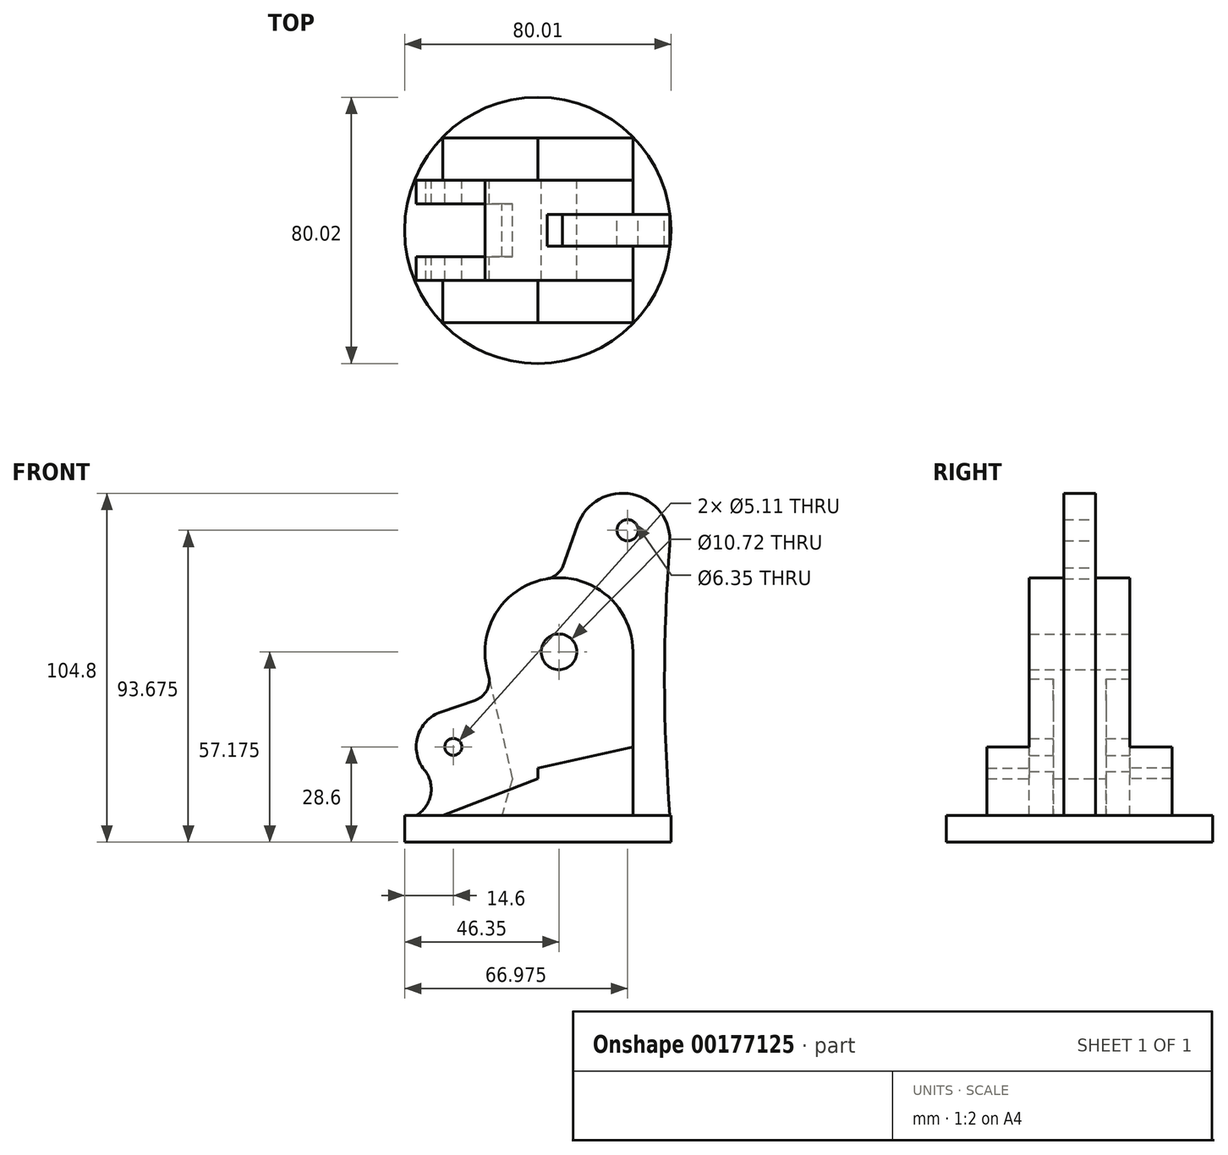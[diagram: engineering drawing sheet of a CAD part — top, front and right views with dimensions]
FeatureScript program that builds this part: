
annotation { "Feature Type Name" : "Feature", "Feature Type Description" : "" }
export const myFeature = defineFeature(function(context is Context, id is Id, definition is map)
    precondition{}
    {
        {
            var Q0;
            Q0=qCreatedBy(makeId("Front.planeOp"),FACE);
            var sketch = newSketch(context, id + "F0", { "sketchPlane" : qUnion([Q0])});
            skCircle(sketch, "E0", {"center": v(14.3, 20.65) * mm, "radius": 2.55 * mm});
            skCircle(sketch, "E1", {"center": v(46.05, 49.23) * mm, "radius": 5.36 * mm});
            skArc(sketch, "E2", {"start": v(68.28, 49.23) * mm, "mid": v(43.53, 71.3) * mm, "end": v(24.4, 44.23) * mm});
            skArc(sketch, "E3", {"start": v(10.72, 31.18) * mm, "mid": v(3.53, 23.44) * mm, "end": v(6.05, 13.19) * mm});
            skArc(sketch, "E4", {"start": v(3.17, 0) * mm, "mid": v(7.58, 6.64) * mm, "end": v(5.2, 14.26) * mm});
            skArc(sketch, "E5", {"start": v(20.84, 34.63) * mm, "mid": v(24.07, 37.1) * mm, "end": v(25.13, 41.02) * mm});
            skArc(sketch, "E6", {"start": v(42.37, 71.14) * mm, "mid": v(42.43, 71.15) * mm, "end": v(42.5, 71.16) * mm});
            skLineSegment(sketch, "E7", {"start": v(20.84, 34.63) * mm, "end": v(10.72, 31.18) * mm});
            skLineSegment(sketch, "E8", {"start": v(3.17, 0) * mm, "end": v(68.28, 0) * mm});
            skLineSegment(sketch, "E9", {"start": v(68.28, 49.23) * mm, "end": v(68.28, 0) * mm});
            skPoint(sketch, "E10.center.orphan", {"position": v(66.68, 85.73) * mm});
            skPoint(sketch, "E11.center.orphan", {"position": v(65.1, 82.55) * mm});
            skPoint(sketch, "E12.end.orphan", {"position": v(79.4, 0) * mm});
            skLineSegment(sketch, "E13", {"start": v(24.4, 44.23) * mm, "end": v(25.13, 41.02) * mm});
            skSolve(sketch);
        }
        {
            var Q0;
            Q0 = qSketchRegion(id + "F0", true);
            extrude(context, id + "F1", {"entities" : qUnion([Q0]), "endBound" : BoundingType.SYMMETRIC, "depth" : 30.18 * mm});
        }
        {
            var Q0;
            Q0=qCreatedBy(makeId("Front.planeOp"),FACE);
            var sketch = newSketch(context, id + "F2", { "sketchPlane" : qUnion([Q0])});
            skArc(sketch, "E14", {"start": v(42.5, 71.16) * mm, "mid": v(27.6, 61.62) * mm, "end": v(24.4, 44.23) * mm});
            skCircle(sketch, "E15", {"center": v(46.05, 49.23) * mm, "radius": 5.36 * mm});
            skArc(sketch, "E16", {"start": v(79.36, 81.41) * mm, "mid": v(68.1, 96.53) * mm, "end": v(51.63, 87.36) * mm});
            skArc(sketch, "E17", {"start": v(42.37, 71.14) * mm, "mid": v(45.77, 72.81) * mm, "end": v(47.62, 76.12) * mm});
            skLineSegment(sketch, "E18", {"start": v(47.03, 74.49) * mm, "end": v(51.63, 87.36) * mm});
            skLineSegment(sketch, "E19", {"start": v(24.4, 44.23) * mm, "end": v(32.04, 11.13) * mm});
            skLineSegment(sketch, "E20", {"start": v(32.04, 11.13) * mm, "end": v(28.86, 0) * mm});
            skPoint(sketch, "E20.startSnap0", {"position": v(33.4, 11.13) * mm});
            skLineSegment(sketch, "E21", {"start": v(28.86, 0) * mm, "end": v(79.4, 0) * mm});
            skArc(sketch, "E22", {"start": v(79.36, 81.41) * mm, "mid": v(77.74, 40.7) * mm, "end": v(79.4, 0) * mm});
            skCircle(sketch, "E23", {"center": v(66.68, 85.73) * mm, "radius": 3.18 * mm});
            skSolve(sketch);
        }
        {
            var Q0;
            Q0 = qSketchRegion(id + "F2", true);
            extrude(context, id + "F3", {"entities" : qUnion([Q0]), "endBound" : BoundingType.SYMMETRIC, "depth" : 9.52 * mm});
        }
        {
            var Q0;
            Q0=makeQuery(id+"FuUQKrlxmKHpC4y_2.opBoolean","SPLIT",BODY,{"disambiguationData":[OD(1.0)],"derivedFrom":makeQuery(id+"F1.opExtrude","SWEPT_BODY",BODY,{"disambiguationData":[OSD([sQuery(id+"F0.wireOp",EDGE,"E0"),sQuery(id+"F0.wireOp",EDGE,"E1"),sQuery(id+"F0.wireOp",EDGE,"E2"),sQuery(id+"F0.wireOp",EDGE,"E3"),sQuery(id+"F0.wireOp",EDGE,"E4"),sQuery(id+"F0.wireOp",EDGE,"E5"),sQuery(id+"F0.wireOp",EDGE,"E7"),sQuery(id+"F0.wireOp",EDGE,"E8"),sQuery(id+"F0.wireOp",EDGE,"E9")])]})});
            var Q1;
            Q1=makeQuery(id+"F3.opExtrude","SWEPT_BODY",BODY,{"disambiguationData":[OSD([sQuery(id+"F2.wireOp",EDGE,"E14"),sQuery(id+"F2.wireOp",EDGE,"E15"),sQuery(id+"F2.wireOp",EDGE,"E16"),sQuery(id+"F2.wireOp",EDGE,"v1n4FTZU-1KL7-gOBp-Gjty-Z9ABf34RUHKt"),sQuery(id+"F2.wireOp",EDGE,"E17"),sQuery(id+"F2.wireOp",EDGE,"E18"),sQuery(id+"F2.wireOp",EDGE,"E19"),sQuery(id+"F2.wireOp",EDGE,"E20"),sQuery(id+"F2.wireOp",EDGE,"E21"),sQuery(id+"F2.wireOp",EDGE,"E22")])]});
            var Q2;
            Q2=makeQuery(id+"FuUQKrlxmKHpC4y_2.opBoolean","SPLIT",BODY,{"disambiguationData":[OD(0.0)],"derivedFrom":makeQuery(id+"F1.opExtrude","SWEPT_BODY",BODY,{"disambiguationData":[OSD([sQuery(id+"F0.wireOp",EDGE,"E0"),sQuery(id+"F0.wireOp",EDGE,"E1"),sQuery(id+"F0.wireOp",EDGE,"E2"),sQuery(id+"F0.wireOp",EDGE,"E3"),sQuery(id+"F0.wireOp",EDGE,"E4"),sQuery(id+"F0.wireOp",EDGE,"E5"),sQuery(id+"F0.wireOp",EDGE,"E7"),sQuery(id+"F0.wireOp",EDGE,"E8"),sQuery(id+"F0.wireOp",EDGE,"E9")])]})});
            booleanBodies(context, id + "F4", {"operationType" : BooleanOperationType.UNION, "tools" : qUnion([Q0, Q1, Q2])});
        }
        {
            var Q0;
            Q0=makeQuery(id+"F1.opExtrude","CAP_FACE",FACE,{"disambiguationData":[OSD([sQuery(id+"F0.wireOp",EDGE,"E0"),sQuery(id+"F0.wireOp",EDGE,"E1"),sQuery(id+"F0.wireOp",EDGE,"E2"),sQuery(id+"F0.wireOp",EDGE,"E3"),sQuery(id+"F0.wireOp",EDGE,"E4"),sQuery(id+"F0.wireOp",EDGE,"E5"),sQuery(id+"F0.wireOp",EDGE,"E7"),sQuery(id+"F0.wireOp",EDGE,"E8"),sQuery(id+"F0.wireOp",EDGE,"E9")])],"isStart":false});
            var sketch = newSketch(context, id + "F5", { "sketchPlane" : qUnion([Q0])});
            skLineSegment(sketch, "E24", {"start": v(11.13, 0) * mm, "end": v(39.7, 11.13) * mm});
            skLineSegment(sketch, "E25", {"start": v(39.7, 14.3) * mm, "end": v(68.28, 20.65) * mm});
            skLineSegment(sketch, "E26", {"start": v(39.7, 14.3) * mm, "end": v(39.7, 11.13) * mm});
            skSolve(sketch);
        }
        {
            var Q0;
            {var subQ3=sQuery(id+"F5.wireOp",EDGE,"E24");Q0=makeQuery(id+"F5.imprint","IMPRINT",FACE,{"disambiguationData":[TD([[makeQuery(id+"F5.imprint","IMPRINT",EDGE,{"derivedFrom":subQ3}),-1.0]])]});}
            extrude(context, id + "F6", {"entities" : qUnion([Q0]), "depth" : 12.7 * mm});
        }
        {
            var Q0;
            Q0=makeQuery(id+"F6.opExtrude","SWEPT_BODY",BODY,{"disambiguationData":[OSD([sQuery(id+"F0.wireOp",EDGE,"E8"),sQuery(id+"F0.wireOp",EDGE,"E9"),sQuery(id+"F5.wireOp",EDGE,"E24"),sQuery(id+"F5.wireOp",EDGE,"E25"),sQuery(id+"F5.wireOp",EDGE,"E26")])]});
            var Q1;
            Q1=qCreatedBy(makeId("Front.planeOp"),FACE);
            mirror(context, id + "F7", {"operationType" : NewBodyOperationType.ADD, "entities" : qUnion([Q0]), "mirrorPlane" : qUnion([Q1])});
        }
        {
            var Q0;
            Q0=qCreatedBy(makeId("Front.planeOp"),FACE);
            var sketch = newSketch(context, id + "F8", { "sketchPlane" : qUnion([Q0])});
            skLineSegment(sketch, "E27", {"start": v(24.4, 44.23) * mm, "end": v(32.04, 11.13) * mm});
            skLineSegment(sketch, "E28", {"start": v(32.04, 11.13) * mm, "end": v(28.86, 0) * mm});
            skLineSegment(sketch, "E29", {"start": v(32.04, 0) * mm, "end": v(0, 0) * mm});
            skPoint(sketch, "E30.end.orphan", {"position": v(32.04, 0) * mm});
            skPoint(sketch, "E31.orphan", {"position": v(34.6, 0) * mm});
            skLineSegment(sketch, "E32", {"start": v(0, 0) * mm, "end": v(0, 61.26) * mm});
            skLineSegment(sketch, "E33", {"start": v(24.4, 44.23) * mm, "end": v(0, 61.26) * mm});
            skPoint(sketch, "E34.center.orphan", {"position": v(46.05, 49.23) * mm});
            skSolve(sketch);
        }
        {
            var Q0;
            Q0 = qSketchRegion(id + "F8", true);
            extrude(context, id + "F9", {"entities" : qUnion([Q0]), "endBound" : BoundingType.SYMMETRIC, "depth" : 15.88 * mm});
        }
        {
            var Q0;
            Q0=makeQuery(id+"F9.opExtrude","SWEPT_BODY",BODY,{"disambiguationData":[OSD([sQuery(id+"F8.wireOp",EDGE,"E27"),sQuery(id+"F8.wireOp",EDGE,"E28"),sQuery(id+"F8.wireOp",EDGE,"E29"),sQuery(id+"F8.wireOp",EDGE,"E32"),sQuery(id+"F8.wireOp",EDGE,"E33")])]});
            var Q1;
            Q1=makeQuery(id+"F1.opExtrude","SWEPT_BODY",BODY,{"disambiguationData":[OSD([sQuery(id+"F0.wireOp",EDGE,"E0"),sQuery(id+"F0.wireOp",EDGE,"E1"),sQuery(id+"F0.wireOp",EDGE,"E2"),sQuery(id+"F0.wireOp",EDGE,"E3"),sQuery(id+"F0.wireOp",EDGE,"E4"),sQuery(id+"F0.wireOp",EDGE,"E5"),sQuery(id+"F0.wireOp",EDGE,"E7"),sQuery(id+"F0.wireOp",EDGE,"E8"),sQuery(id+"F0.wireOp",EDGE,"E9"),sQuery(id+"F0.wireOp",EDGE,"E13")])]});
            booleanBodies(context, id + "F10", {"operationType" : BooleanOperationType.SUBTRACTION, "tools" : qUnion([Q0]), "targets" : qUnion([Q1])});
        }
        {
            var Q0;
            Q0=qCreatedBy(makeId("Top.planeOp"),FACE);
            var sketch = newSketch(context, id + "F11", { "sketchPlane" : qUnion([Q0])});
            skCircle(sketch, "E35", {"center": v(39.7, 0) * mm, "radius": 40 * mm});
            skSolve(sketch);
        }
        {
            var Q0;
            Q0=makeQuery(id+"F11.imprint","IMPRINT",FACE,{"disambiguationData":[TD([[makeQuery(id+"F11.imprint","IMPRINT",EDGE,{"derivedFrom":sQuery(id+"F11.wireOp",EDGE,"E35")}),1.0]])]});
            extrude(context, id + "F12", {"entities" : qUnion([Q0]), "depth" : 7.95 * mm});
        }
        {
            var Q0;
            Q0=makeQuery(id+"F12.opExtrude","SWEPT_BODY",BODY,{"disambiguationData":[OSD([sQuery(id+"F11.wireOp",EDGE,"E35")])]});
            transform(context, id + "F13", {"entities" : qUnion([Q0]), "transformType" : TransformType.TRANSLATION_3D, "dx" : 0 * mm, "dy" : 0 * mm, "dz" : -7.95 * mm, "makeCopy" : false});
        }
        {
            var Q0;
            Q0=makeQuery(id+"F3.opExtrude","CAP_FACE",FACE,{"disambiguationData":[OSD([sQuery(id+"F2.wireOp",EDGE,"E14"),sQuery(id+"F2.wireOp",EDGE,"E15"),sQuery(id+"F2.wireOp",EDGE,"E16"),sQuery(id+"F2.wireOp",EDGE,"v1n4FTZU-1KL7-gOBp-Gjty-Z9ABf34RUHKt"),sQuery(id+"F2.wireOp",EDGE,"E17"),sQuery(id+"F2.wireOp",EDGE,"E18"),sQuery(id+"F2.wireOp",EDGE,"E19"),sQuery(id+"F2.wireOp",EDGE,"E20"),sQuery(id+"F2.wireOp",EDGE,"E21"),sQuery(id+"F2.wireOp",EDGE,"E22")])],"isStart":false});
            var sketch = newSketch(context, id + "F14", { "sketchPlane" : qUnion([Q0])});
            skCircle(sketch, "E36", {"center": v(66.68, 85.73) * mm, "radius": 9.53 * mm});
            skCircle(sketch, "E37", {"center": v(66.68, 85.73) * mm, "radius": 7.94 * mm});
            skSolve(sketch);
        }
        {
            var Q0;
            Q0 = qSketchRegion(id + "F14", true);
            extrude(context, id + "F15", {"entities" : qUnion([Q0]), "endBound" : BoundingType.SYMMETRIC, "depth" : 3.17 * mm});
        }
        {
            var Q0;
            Q0=makeQuery(id+"F15.opExtrude","SWEPT_BODY",BODY,{"disambiguationData":[OSD([sQuery(id+"F14.wireOp",EDGE,"E36"),sQuery(id+"F14.wireOp",EDGE,"E37")])]});
            var Q1;
            Q1=qCreatedBy(makeId("Front.planeOp"),FACE);
            mirror(context, id + "F16", {"entities" : qUnion([Q0]), "mirrorPlane" : qUnion([Q1])});
        }
        {
            var Q0;
            Q0=makeQuery(id+"F16.opPattern","COPY",BODY,{"derivedFrom":makeQuery(id+"F15.opExtrude","SWEPT_BODY",BODY,{"disambiguationData":[OSD([sQuery(id+"F14.wireOp",EDGE,"E36"),sQuery(id+"F14.wireOp",EDGE,"E37")])]}),"instanceName":"1"});
            var Q1;
            Q1=makeQuery(id+"F15.opExtrude","SWEPT_BODY",BODY,{"disambiguationData":[OSD([sQuery(id+"F14.wireOp",EDGE,"E36"),sQuery(id+"F14.wireOp",EDGE,"E37")])]});
            var Q2;
            Q2=makeQuery(id+"F12.opExtrude","SWEPT_BODY",BODY,{"disambiguationData":[OSD([sQuery(id+"F11.wireOp",EDGE,"E35")])]});
            booleanBodies(context, id + "F17", {"operationType" : BooleanOperationType.SUBTRACTION, "tools" : qUnion([Q0, Q1]), "targets" : qUnion([Q2])});
        }
    });
